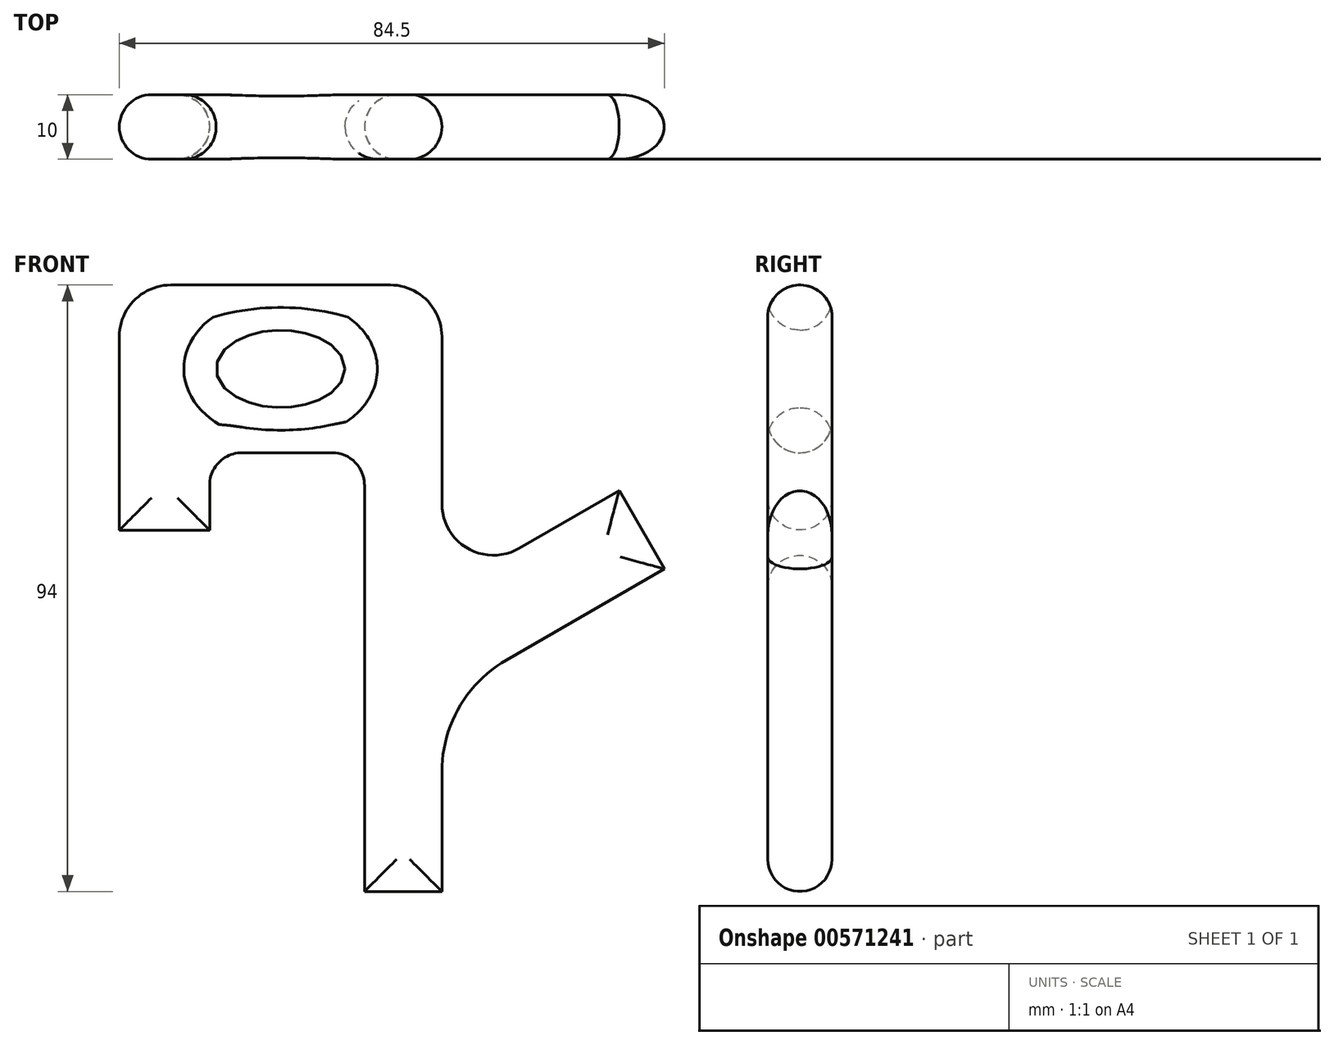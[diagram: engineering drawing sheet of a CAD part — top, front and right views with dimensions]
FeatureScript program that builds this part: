
annotation { "Feature Type Name" : "Feature", "Feature Type Description" : "" }
export const myFeature = defineFeature(function(context is Context, id is Id, definition is map)
    precondition{}
    {
        {
            var Q0;
            Q0=qCreatedBy(makeId("Front.planeOp"),FACE);
            var sketch = newSketch(context, id + "F0", { "sketchPlane" : qUnion([Q0])});
            skEllipse(sketch, "E0", {"center": v(0, 0) * mm, "majorRadius": 10 * mm, "minorRadius": 6 * mm, "majorAxis": v(1, 0)});
            skLineSegment(sketch, "E1", {"start": v(17, 13) * mm, "end": v(-17, 13) * mm});
            skLineSegment(sketch, "E2", {"start": v(-25, 5) * mm, "end": v(-25, -25) * mm});
            skLineSegment(sketch, "E3", {"start": v(-25, -25) * mm, "end": v(-11, -25) * mm});
            skLineSegment(sketch, "E4", {"start": v(-11, -25) * mm, "end": v(-11, -18) * mm});
            skLineSegment(sketch, "E5", {"start": v(-6, -13) * mm, "end": v(8, -13) * mm});
            skLineSegment(sketch, "E6", {"start": v(13, -18) * mm, "end": v(13, -81) * mm});
            skLineSegment(sketch, "E7", {"start": v(13, -81) * mm, "end": v(25, -81) * mm});
            skLineSegment(sketch, "E8", {"start": v(25, 5) * mm, "end": v(25, -20.9) * mm});
            skLineSegment(sketch, "E9", {"start": v(25, -42.84) * mm, "end": v(56, -24.94) * mm, "construction": true});
            skLineSegment(sketch, "E10", {"start": v(56, -24.94) * mm, "end": v(59.5, -31) * mm});
            skLineSegment(sketch, "E11", {"start": v(59.5, -31) * mm, "end": v(35, -45.15) * mm});
            skLineSegment(sketch, "E12", {"start": v(56, -24.94) * mm, "end": v(52.5, -18.88) * mm});
            skLineSegment(sketch, "E13", {"start": v(52.5, -18.88) * mm, "end": v(37, -27.82) * mm});
            skPoint(sketch, "E14.newPointA", {"position": v(25, -81) * mm});
            skArc(sketch, "E14.filletArc", {"start": v(25, -20.9) * mm, "mid": v(29, -27.82) * mm, "end": v(37, -27.82) * mm});
            skLineSegment(sketch, "E15", {"start": v(25, -81) * mm, "end": v(25, -62.47) * mm});
            skPoint(sketch, "E16.visualSharp", {"position": v(25, -50.92) * mm});
            skArc(sketch, "E16.filletArc", {"start": v(35, -45.15) * mm, "mid": v(27.68, -52.47) * mm, "end": v(25, -62.47) * mm});
            skPoint(sketch, "E17.visualSharp", {"position": v(25, 13) * mm});
            skArc(sketch, "E17.filletArc", {"start": v(25, 5) * mm, "mid": v(22.66, 10.66) * mm, "end": v(17, 13) * mm});
            skPoint(sketch, "E18.visualSharp", {"position": v(-25, 13) * mm});
            skArc(sketch, "E18.filletArc", {"start": v(-17, 13) * mm, "mid": v(-22.66, 10.66) * mm, "end": v(-25, 5) * mm});
            skPoint(sketch, "E19.visualSharp", {"position": v(13, -13) * mm});
            skArc(sketch, "E19.filletArc", {"start": v(13, -18) * mm, "mid": v(11.54, -14.46) * mm, "end": v(8, -13) * mm});
            skPoint(sketch, "E20.visualSharp", {"position": v(-11, -13) * mm});
            skArc(sketch, "E20.filletArc", {"start": v(-6, -13) * mm, "mid": v(-9.54, -14.46) * mm, "end": v(-11, -18) * mm});
            skSolve(sketch);
        }
        {
            var Q0;
            Q0=makeQuery(id+"F0.imprint","IMPRINT",FACE,{"disambiguationData":[TD([[makeQuery(id+"F0.imprint","IMPRINT",EDGE,{"derivedFrom":sQuery(id+"F0.wireOp",EDGE,"E0")}),-1.0]])]});
            extrude(context, id + "F1", {"entities" : qUnion([Q0]), "depth" : 10 * mm, "offsetDistance" : 25 * mm});
        }
        {
            var Q0;
            Q0=makeQuery(id+"F1.opExtrude","CAP_FACE",FACE,{"disambiguationData":[OSD([sQuery(id+"F0.wireOp",EDGE,"E0"),sQuery(id+"F0.wireOp",EDGE,"E1"),sQuery(id+"F0.wireOp",EDGE,"E2"),sQuery(id+"F0.wireOp",EDGE,"E3"),sQuery(id+"F0.wireOp",EDGE,"E4"),sQuery(id+"F0.wireOp",EDGE,"E5"),sQuery(id+"F0.wireOp",EDGE,"E6"),sQuery(id+"F0.wireOp",EDGE,"E7"),sQuery(id+"F0.wireOp",EDGE,"E8"),sQuery(id+"F0.wireOp",EDGE,"E10"),sQuery(id+"F0.wireOp",EDGE,"E11"),sQuery(id+"F0.wireOp",EDGE,"E12"),sQuery(id+"F0.wireOp",EDGE,"E13"),sQuery(id+"F0.wireOp",EDGE,"E14.filletArc"),sQuery(id+"F0.wireOp",EDGE,"E15"),sQuery(id+"F0.wireOp",EDGE,"E16.filletArc"),sQuery(id+"F0.wireOp",EDGE,"E17.filletArc"),sQuery(id+"F0.wireOp",EDGE,"E18.filletArc"),sQuery(id+"F0.wireOp",EDGE,"E19.filletArc"),sQuery(id+"F0.wireOp",EDGE,"E20.filletArc")])],"isStart":false});
            var Q1;
            Q1=makeQuery(id+"F1.opExtrude","CAP_FACE",FACE,{"disambiguationData":[OSD([sQuery(id+"F0.wireOp",EDGE,"E0"),sQuery(id+"F0.wireOp",EDGE,"E1"),sQuery(id+"F0.wireOp",EDGE,"E2"),sQuery(id+"F0.wireOp",EDGE,"E3"),sQuery(id+"F0.wireOp",EDGE,"E4"),sQuery(id+"F0.wireOp",EDGE,"E5"),sQuery(id+"F0.wireOp",EDGE,"E6"),sQuery(id+"F0.wireOp",EDGE,"E7"),sQuery(id+"F0.wireOp",EDGE,"E8"),sQuery(id+"F0.wireOp",EDGE,"E10"),sQuery(id+"F0.wireOp",EDGE,"E11"),sQuery(id+"F0.wireOp",EDGE,"E12"),sQuery(id+"F0.wireOp",EDGE,"E13"),sQuery(id+"F0.wireOp",EDGE,"E14.filletArc"),sQuery(id+"F0.wireOp",EDGE,"E15"),sQuery(id+"F0.wireOp",EDGE,"E16.filletArc"),sQuery(id+"F0.wireOp",EDGE,"E17.filletArc"),sQuery(id+"F0.wireOp",EDGE,"E18.filletArc"),sQuery(id+"F0.wireOp",EDGE,"E19.filletArc"),sQuery(id+"F0.wireOp",EDGE,"E20.filletArc")])],"isStart":true});
            fillet(context, id + "F2", {"entities" : qUnion([Q0, Q1]), "radius" : 5 * mm, "tangentPropagation" : true, "allowEdgeOverflow" : false});
        }
    });
